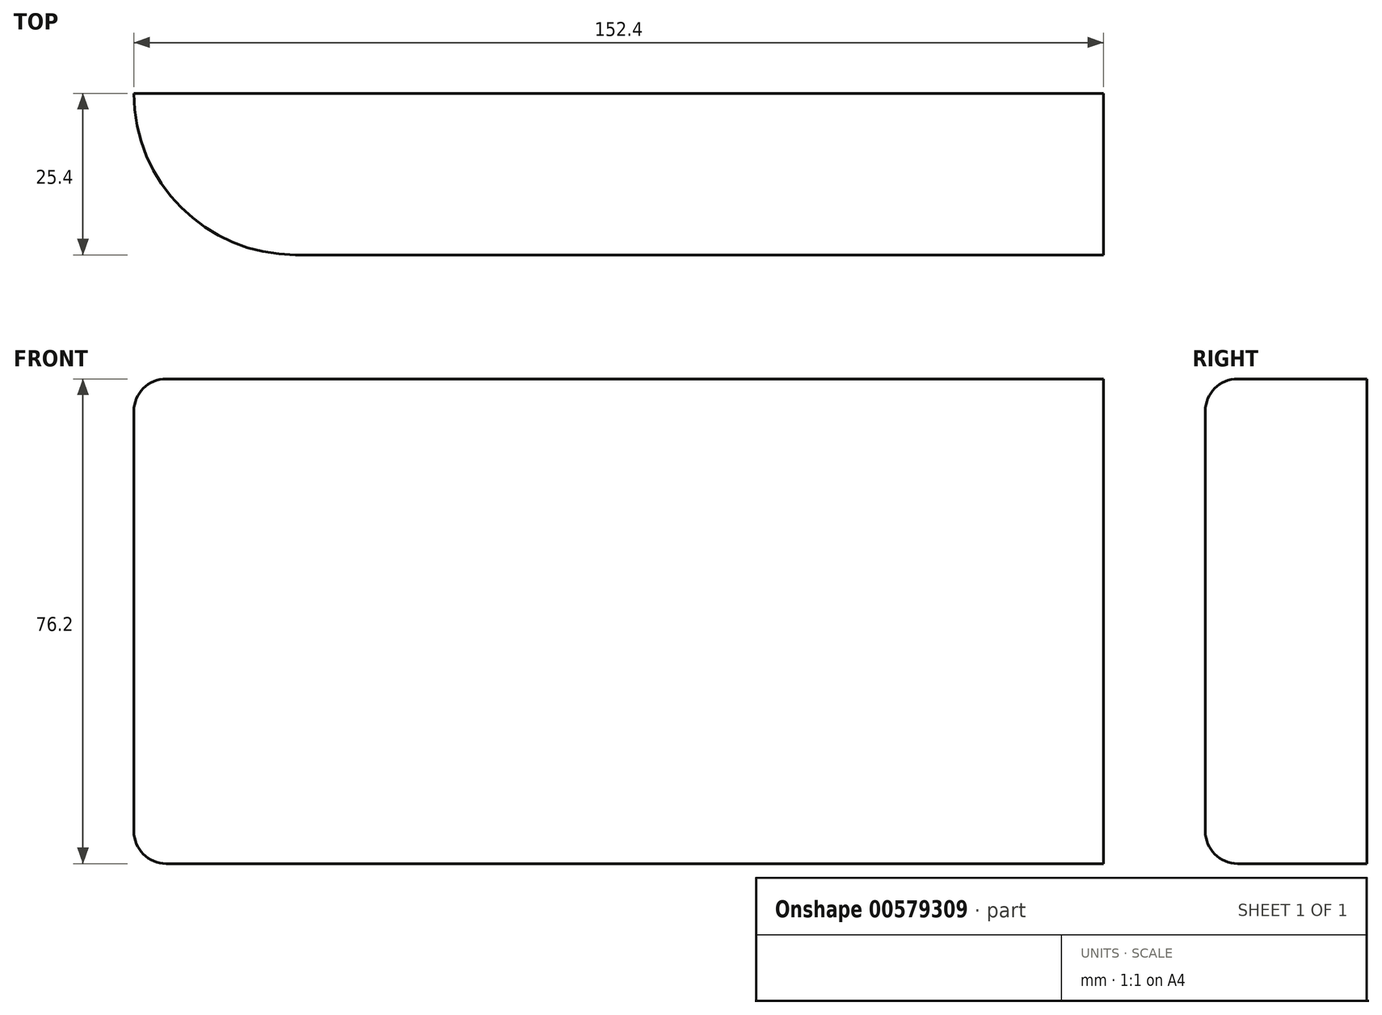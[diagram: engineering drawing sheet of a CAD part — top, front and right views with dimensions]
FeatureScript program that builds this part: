
annotation { "Feature Type Name" : "Feature", "Feature Type Description" : "" }
export const myFeature = defineFeature(function(context is Context, id is Id, definition is map)
    precondition{}
    {
        {
            var Q0;
            Q0=qCreatedBy(makeId("Top.planeOp"),FACE);
            var sketch = newSketch(context, id + "F0", { "sketchPlane" : qUnion([Q0])});
            skLineSegment(sketch, "E0.bottom", {"start": v(-73.24, 29.01) * mm, "end": v(53.76, 29.01) * mm});
            skLineSegment(sketch, "E0.top", {"start": v(-73.24, 3.61) * mm, "end": v(53.76, 3.61) * mm});
            skLineSegment(sketch, "E0.left", {"start": v(-73.24, 29.01) * mm, "end": v(-73.24, 3.61) * mm});
            skLineSegment(sketch, "E0.right", {"start": v(53.76, 29.01) * mm, "end": v(53.76, 3.61) * mm});
            skLineSegment(sketch, "E1", {"start": v(-73.24, 29.01) * mm, "end": v(-98.64, 29.01) * mm});
            skArc(sketch, "E2", {"start": v(-98.64, 29.01) * mm, "mid": v(-91.2, 11.05) * mm, "end": v(-73.24, 3.61) * mm});
            skSolve(sketch);
        }
        {
            var Q0;
            Q0=makeQuery(id+"F0.imprint","IMPRINT",FACE,{"disambiguationData":[TD([[makeQuery(id+"F0.imprint","IMPRINT",EDGE,{"derivedFrom":sQuery(id+"F0.wireOp",EDGE,"E0.left")}),-1.0]])]});
            var Q1;
            Q1=makeQuery(id+"F0.imprint","IMPRINT",FACE,{"disambiguationData":[TD([[makeQuery(id+"F0.imprint","IMPRINT",EDGE,{"derivedFrom":sQuery(id+"F0.wireOp",EDGE,"E0.bottom")}),-1.0]])]});
            extrude(context, id + "F1", {"entities" : qUnion([Q0, Q1]), "depth" : 25.4 * mm, "offsetDistance" : 25.4 * mm});
        }
        {
            var Q0;
            Q0=makeQuery(id+"F1.opExtrude","CAP_FACE",FACE,{"disambiguationData":[OSD([sQuery(id+"F0.wireOp",EDGE,"E0.bottom"),sQuery(id+"F0.wireOp",EDGE,"E0.top"),sQuery(id+"F0.wireOp",EDGE,"E0.right"),sQuery(id+"F0.wireOp",EDGE,"E1"),sQuery(id+"F0.wireOp",EDGE,"E2")])],"isStart":false});
            extrude(context, id + "F2", {"entities" : qUnion([Q0]), "operationType" : NewBodyOperationType.ADD, "depth" : 50.8 * mm, "offsetDistance" : 25.4 * mm});
        }
        {
            var Q0;
            Q0=makeQuery(id+"F2.opExtrude","CAP_EDGE",EDGE,{"disambiguationData":[OSD([sQuery(id+"F0.wireOp",EDGE,"E2")])],"isStart":false});
            var Q1;
            Q1=makeQuery(id+"F1.opExtrude","CAP_EDGE",EDGE,{"disambiguationData":[OSD([sQuery(id+"F0.wireOp",EDGE,"E2")])],"isStart":true});
            fillet(context, id + "F3", {"entities" : qUnion([Q0, Q1]), "radius" : 5.08 * mm, "tangentPropagation" : true, "allowEdgeOverflow" : false});
        }
    });
